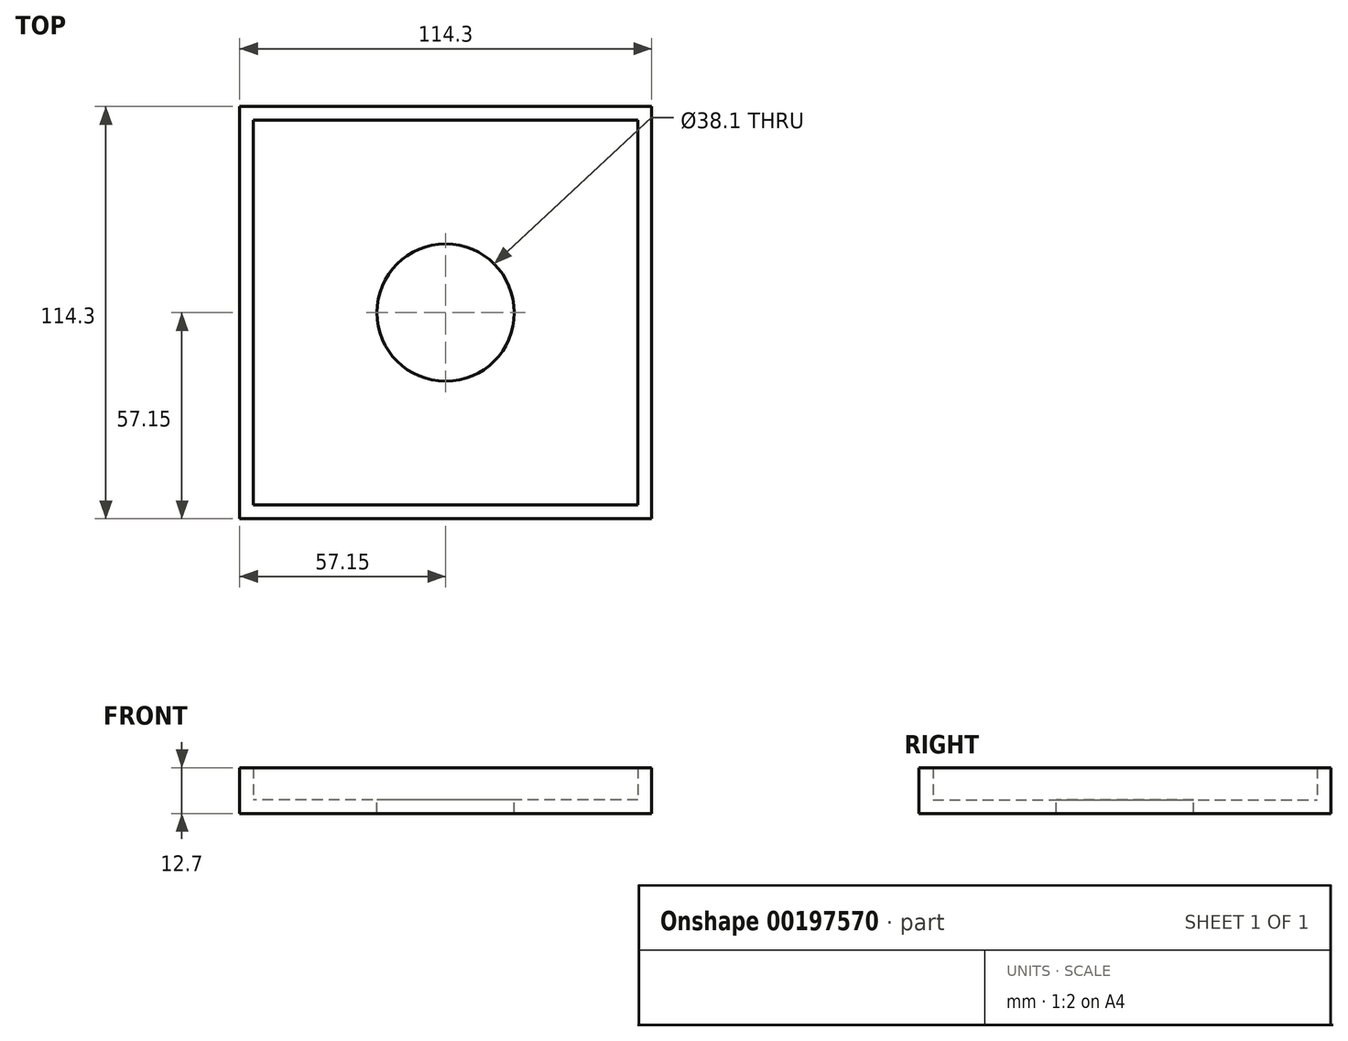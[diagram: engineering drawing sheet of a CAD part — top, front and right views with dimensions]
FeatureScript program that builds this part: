
annotation { "Feature Type Name" : "Feature", "Feature Type Description" : "" }
export const myFeature = defineFeature(function(context is Context, id is Id, definition is map)
    precondition{}
    {
        {
            var Q0;
            Q0=qCreatedBy(makeId("Top.planeOp"),FACE);
            var sketch = newSketch(context, id + "F0", { "sketchPlane" : qUnion([Q0])});
            skLineSegment(sketch, "E0.bottom", {"start": v(-57.15, 57.15) * mm, "end": v(57.15, 57.15) * mm});
            skLineSegment(sketch, "E0.top", {"start": v(-57.15, -57.15) * mm, "end": v(57.15, -57.15) * mm});
            skLineSegment(sketch, "E0.left", {"start": v(-57.15, 57.15) * mm, "end": v(-57.15, -57.15) * mm});
            skLineSegment(sketch, "E0.right", {"start": v(57.15, 57.15) * mm, "end": v(57.15, -57.15) * mm});
            skPoint(sketch, "E0.middle", {"position": v(0, 0) * mm});
            skLineSegment(sketch, "E1.bottom", {"start": v(-53.34, 53.34) * mm, "end": v(53.34, 53.34) * mm});
            skLineSegment(sketch, "E1.top", {"start": v(-53.34, -53.34) * mm, "end": v(53.34, -53.34) * mm});
            skLineSegment(sketch, "E1.left", {"start": v(-53.34, 53.34) * mm, "end": v(-53.34, -53.34) * mm});
            skLineSegment(sketch, "E1.right", {"start": v(53.34, 53.34) * mm, "end": v(53.34, -53.34) * mm});
            skSolve(sketch);
        }
        {
            var Q0;
            Q0 = qSketchRegion(id + "F0", true);
            var Q1;
            Q1=makeQuery(id+"F0.imprint","IMPRINT",FACE,{"disambiguationData":[TD([[makeQuery(id+"F0.imprint","IMPRINT",EDGE,{"derivedFrom":sQuery(id+"F0.wireOp",EDGE,"E1.bottom")}),-1.0]])]});
            extrude(context, id + "F1", {"entities" : qUnion([Q0, Q1]), "depth" : 3.8 * mm});
        }
        {
            var Q0;
            Q0=makeQuery(id+"F0.imprint","IMPRINT",FACE,{"disambiguationData":[TD([[makeQuery(id+"F0.imprint","IMPRINT",EDGE,{"derivedFrom":sQuery(id+"F0.wireOp",EDGE,"E0.bottom")}),-1.0]])]});
            extrude(context, id + "F2", {"entities" : qUnion([Q0]), "operationType" : NewBodyOperationType.ADD, "depth" : 12.7 * mm});
        }
        {
            var Q0;
            Q0=makeQuery(id+"F1.opExtrude","CAP_FACE",FACE,{"disambiguationData":[OSD([sQuery(id+"F0.wireOp",EDGE,"E0.bottom"),sQuery(id+"F0.wireOp",EDGE,"E0.top"),sQuery(id+"F0.wireOp",EDGE,"E0.left"),sQuery(id+"F0.wireOp",EDGE,"E0.right")])],"isStart":false});
            var sketch = newSketch(context, id + "F3", { "sketchPlane" : qUnion([Q0])});
            skSolve(sketch);
        }
        {
            var Q0;
            {var subQ0=makeQuery(id+"F1.opExtrude","CAP_FACE",FACE,{"disambiguationData":[OSD([sQuery(id+"F0.wireOp",EDGE,"E0.bottom"),sQuery(id+"F0.wireOp",EDGE,"E0.top"),sQuery(id+"F0.wireOp",EDGE,"E0.left"),sQuery(id+"F0.wireOp",EDGE,"E0.right")])],"isStart":false});Q0=makeQuery(id+"F3.imprint","IMPRINT",FACE,{"disambiguationData":[TD([[makeQuery(id+"F3.imprint","IMPRINT",EDGE,{"derivedFrom":makeQuery(id+"F2.boolean.opBoolean","INTERSECT",EDGE,{"derivedFrom":[subQ0,makeQuery(id+"F2.opExtrude","SWEPT_FACE",FACE,{"disambiguationData":[OSD([sQuery(id+"F0.wireOp",EDGE,"E1.bottom")])]})]})}),1.0]])]});}
            var sketch = newSketch(context, id + "F4", { "sketchPlane" : qUnion([Q0])});
            skCircle(sketch, "E2", {"center": v(0, 0) * mm, "radius": 19.05 * mm});
            skSolve(sketch);
        }
        {
            var Q0;
            Q0 = qSketchRegion(id + "F4", true);
            extrude(context, id + "F5", {"entities" : qUnion([Q0]), "operationType" : NewBodyOperationType.REMOVE, "oppositeDirection" : true, "depth" : 6.86 * mm});
        }
    });
